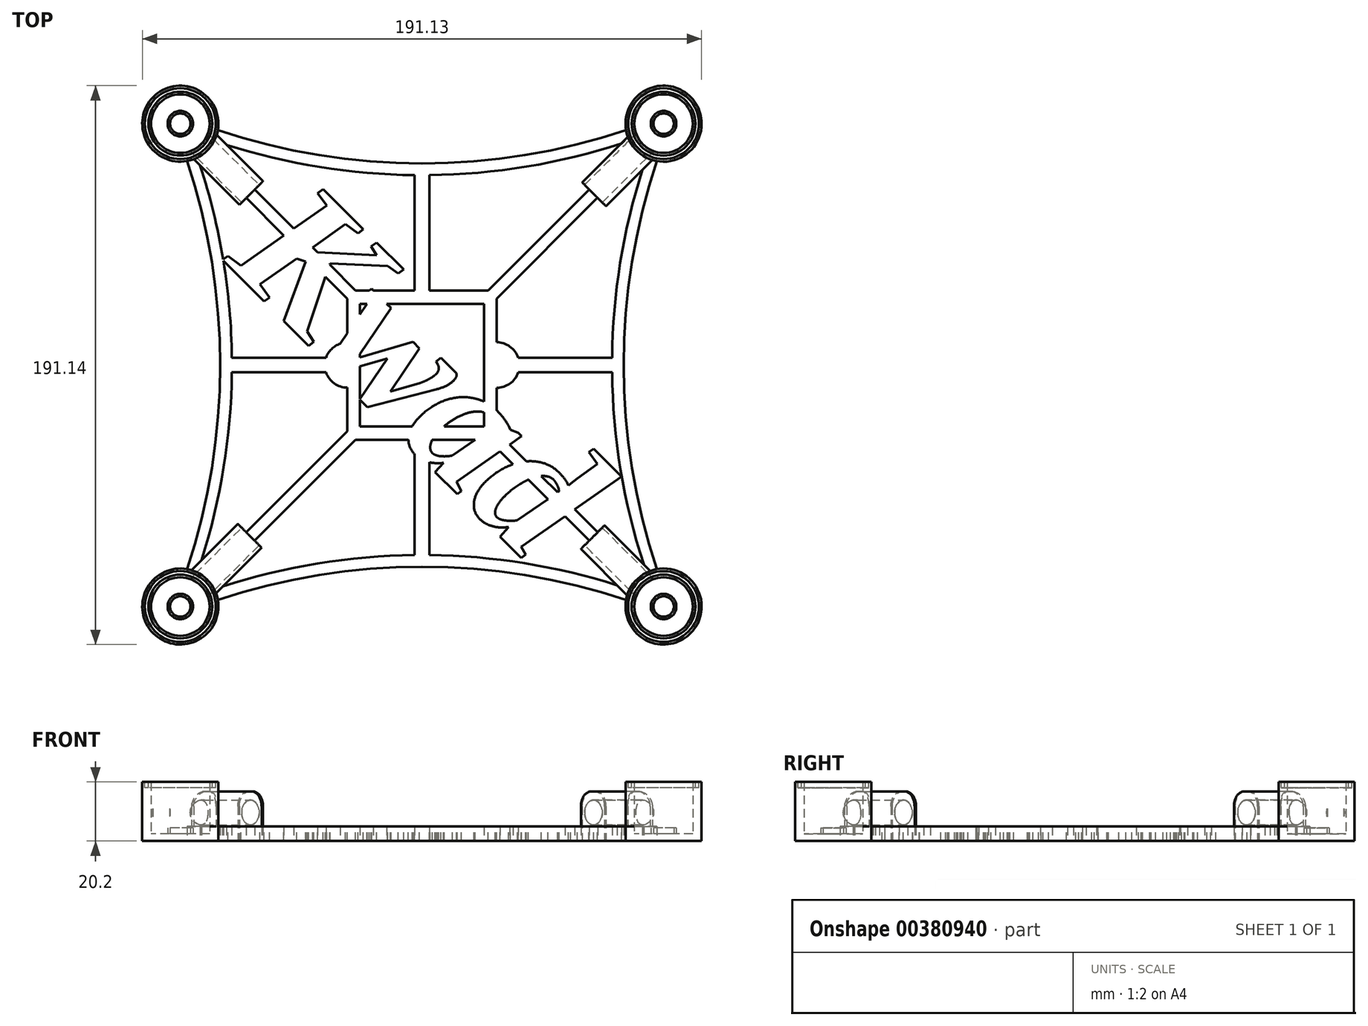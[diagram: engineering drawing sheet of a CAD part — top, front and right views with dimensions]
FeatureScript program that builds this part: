
annotation { "Feature Type Name" : "Feature", "Feature Type Description" : "" }
export const myFeature = defineFeature(function(context is Context, id is Id, definition is map)
    precondition{}
    {
        {
            var Q0;
            Q0=qCreatedBy(makeId("Top.planeOp"),FACE);
            var sketch = newSketch(context, id + "F0", { "sketchPlane" : qUnion([Q0])});
            skLineSegment(sketch, "E0.bottom", {"start": v(25.5, -25.5) * mm, "end": v(-25.5, -25.5) * mm});
            skLineSegment(sketch, "E0.top", {"start": v(25.5, 25.5) * mm, "end": v(-25.5, 25.5) * mm});
            skLineSegment(sketch, "E0.left", {"start": v(25.5, -25.5) * mm, "end": v(25.5, -7.8) * mm});
            skLineSegment(sketch, "E0.right", {"start": v(-25.5, -25.5) * mm, "end": v(-25.5, -7.7) * mm});
            skPoint(sketch, "E0.middle", {"position": v(0, 0) * mm});
            skCircle(sketch, "E1", {"center": v(-82.55, -82.57) * mm, "radius": 10 * mm});
            skArc(sketch, "E2", {"start": v(-70.95, -76.72) * mm, "mid": v(-73.36, -73.38) * mm, "end": v(-76.7, -70.96) * mm});
            skCircle(sketch, "E3", {"center": v(-82.55, -82.57) * mm, "radius": 3.5 * mm});
            skCircle(sketch, "E4", {"center": v(-82.55, -82.57) * mm, "radius": 4.36 * mm});
            skCircle(sketch, "E5.1.0", {"center": v(82.58, -82.57) * mm, "radius": 4.36 * mm});
            skArc(sketch, "E5.1.1", {"start": v(69.78, -80.31) * mm, "mid": v(91.78, -91.76) * mm, "end": v(80.33, -69.77) * mm});
            skCircle(sketch, "E5.1.2", {"center": v(82.58, -82.57) * mm, "radius": 3.5 * mm});
            skCircle(sketch, "E5.1.3", {"center": v(82.58, -82.57) * mm, "radius": 10 * mm});
            skCircle(sketch, "E5.2.0", {"center": v(82.58, 82.57) * mm, "radius": 4.36 * mm});
            skArc(sketch, "E5.2.1", {"start": v(80.33, 69.77) * mm, "mid": v(91.78, 91.76) * mm, "end": v(69.78, 80.31) * mm});
            skCircle(sketch, "E5.2.2", {"center": v(82.58, 82.57) * mm, "radius": 3.5 * mm});
            skCircle(sketch, "E5.2.3", {"center": v(82.58, 82.57) * mm, "radius": 10 * mm});
            skCircle(sketch, "E5.3.0", {"center": v(-82.55, 82.57) * mm, "radius": 4.36 * mm});
            skArc(sketch, "E5.3.1", {"start": v(-69.75, 80.31) * mm, "mid": v(-91.75, 91.76) * mm, "end": v(-80.3, 69.77) * mm});
            skCircle(sketch, "E5.3.2", {"center": v(-82.55, 82.57) * mm, "radius": 3.5 * mm});
            skCircle(sketch, "E5.3.3", {"center": v(-82.55, 82.57) * mm, "radius": 10 * mm});
            skPoint(sketch, "E5.center", {"position": v(0.01, 0) * mm});
            skPoint(sketch, "E6.endSnap0", {"position": v(-25.5, 0) * mm});
            skArc(sketch, "E7.trimOffspring", {"start": v(-70.95, 76.72) * mm, "mid": v(-37.18, 68.12) * mm, "end": v(-2.49, 64.97) * mm});
            skArc(sketch, "E8.trimOffspring", {"start": v(-69.75, 80.31) * mm, "mid": v(0.01, 68.95) * mm, "end": v(69.78, 80.31) * mm});
            skArc(sketch, "E9.trimOffspring", {"start": v(-80.3, -69.77) * mm, "mid": v(-68.94, 0) * mm, "end": v(-80.3, 69.77) * mm});
            skArc(sketch, "E10.trimOffspring", {"start": v(-76.7, -70.96) * mm, "mid": v(-68.1, -37.2) * mm, "end": v(-64.95, -2.5) * mm});
            skArc(sketch, "E11.trimOffspring", {"start": v(80.33, 69.77) * mm, "mid": v(68.96, 0) * mm, "end": v(80.33, -69.77) * mm});
            skArc(sketch, "E12.trimOffspring", {"start": v(76.73, 70.96) * mm, "mid": v(68.13, 37.2) * mm, "end": v(64.98, 2.5) * mm});
            skArc(sketch, "E13.trimOffspring", {"start": v(70.97, -76.72) * mm, "mid": v(37.21, -68.12) * mm, "end": v(2.51, -64.96) * mm});
            skArc(sketch, "E14.trimOffspring", {"start": v(69.78, -80.31) * mm, "mid": v(0.01, -68.95) * mm, "end": v(-69.75, -80.31) * mm});
            skArc(sketch, "E15.trimOffspring", {"start": v(76.73, -70.96) * mm, "mid": v(73.4, -73.38) * mm, "end": v(70.97, -76.72) * mm});
            skArc(sketch, "E16.trimOffspring", {"start": v(-80.3, -69.77) * mm, "mid": v(-91.75, -91.76) * mm, "end": v(-69.75, -80.31) * mm});
            skArc(sketch, "E17.trimOffspring", {"start": v(70.97, 76.72) * mm, "mid": v(73.4, 73.38) * mm, "end": v(76.73, 70.96) * mm});
            skArc(sketch, "E18.trimOffspring", {"start": v(-76.7, 70.96) * mm, "mid": v(-73.36, 73.38) * mm, "end": v(-70.95, 76.72) * mm});
            skLineSegment(sketch, "E19.0", {"start": v(-25.47, 2.5) * mm, "end": v(-25.5, 2.5) * mm});
            skLineSegment(sketch, "E20.0", {"start": v(-25.47, -2.5) * mm, "end": v(-25.5, -2.5) * mm});
            skLineSegment(sketch, "E21.1.0", {"start": v(-2.49, -25.49) * mm, "end": v(-2.49, -64.96) * mm});
            skLineSegment(sketch, "E21.1.1", {"start": v(2.51, -25.49) * mm, "end": v(2.51, -64.96) * mm});
            skLineSegment(sketch, "E21.2.0", {"start": v(32.9, -2.5) * mm, "end": v(64.98, -2.5) * mm});
            skLineSegment(sketch, "E21.2.1", {"start": v(32.9, 2.5) * mm, "end": v(64.98, 2.5) * mm});
            skLineSegment(sketch, "E21.3.0", {"start": v(2.51, 25.49) * mm, "end": v(2.51, 64.97) * mm});
            skLineSegment(sketch, "E21.3.1", {"start": v(-2.49, 25.49) * mm, "end": v(-2.49, 64.97) * mm});
            skArc(sketch, "E22.trimOffspring", {"start": v(-64.95, 2.5) * mm, "mid": v(-68.1, 37.2) * mm, "end": v(-76.7, 70.96) * mm});
            skArc(sketch, "E23.trimOffspring", {"start": v(64.98, -2.5) * mm, "mid": v(68.13, -37.2) * mm, "end": v(76.73, -70.96) * mm});
            skArc(sketch, "E24.trimOffspring", {"start": v(2.51, 64.97) * mm, "mid": v(37.21, 68.12) * mm, "end": v(70.97, 76.72) * mm});
            skArc(sketch, "E25.trimOffspring", {"start": v(-2.49, -64.96) * mm, "mid": v(-37.18, -68.12) * mm, "end": v(-70.95, -76.72) * mm});
            skLineSegment(sketch, "E26.bottom", {"start": v(21.19, -20.94) * mm, "end": v(-21.16, -20.94) * mm});
            skLineSegment(sketch, "E26.top", {"start": v(21.19, 20.94) * mm, "end": v(-21.16, 20.94) * mm});
            skLineSegment(sketch, "E26.left", {"start": v(21.19, -20.94) * mm, "end": v(21.19, 20.94) * mm});
            skLineSegment(sketch, "E26.right", {"start": v(-21.16, -20.94) * mm, "end": v(-21.16, 20.94) * mm});
            skArc(sketch, "E27", {"start": v(-25.5, 7.7) * mm, "mid": v(-29.97, 6.27) * mm, "end": v(-32.78, 2.5) * mm});
            skArc(sketch, "E28", {"start": v(25.5, 7.8) * mm, "mid": v(30.05, 6.34) * mm, "end": v(32.9, 2.5) * mm});
            skLineSegment(sketch, "E29.trimOffspring", {"start": v(-32.78, 2.5) * mm, "end": v(-64.95, 2.5) * mm});
            skLineSegment(sketch, "E30.trimOffspring", {"start": v(-32.78, -2.5) * mm, "end": v(-64.95, -2.5) * mm});
            skLineSegment(sketch, "E31.trimOffspring", {"start": v(-25.5, 7.7) * mm, "end": v(-25.5, 25.5) * mm});
            skArc(sketch, "E32.trimOffspring", {"start": v(-32.78, -2.5) * mm, "mid": v(-29.97, -6.27) * mm, "end": v(-25.5, -7.7) * mm});
            skLineSegment(sketch, "E33.trimOffspring", {"start": v(25.5, 7.8) * mm, "end": v(25.5, 25.5) * mm});
            skPoint(sketch, "E34.orphan", {"position": v(25.5, -2.5) * mm});
            skPoint(sketch, "E35.orphan", {"position": v(25.5, 2.5) * mm});
            skArc(sketch, "E36.trimOffspring", {"start": v(32.9, -2.5) * mm, "mid": v(30.05, -6.34) * mm, "end": v(25.5, -7.8) * mm});
            skSolve(sketch);
        }
        {
            var Q0;
            Q0=makeQuery(id+"F0.imprint","IMPRINT",FACE,{"disambiguationData":[TD([[makeQuery(id+"F0.imprint","IMPRINT",EDGE,{"derivedFrom":sQuery(id+"F0.wireOp",EDGE,"E1")}),-1.0]])]});
            var Q1;
            Q1=makeQuery(id+"F0.imprint","IMPRINT",FACE,{"disambiguationData":[TD([[makeQuery(id+"F0.imprint","IMPRINT",EDGE,{"derivedFrom":sQuery(id+"F0.wireOp",EDGE,"E26.bottom")}),1.0]])]});
            extrude(context, id + "F1", {"entities" : qUnion([Q0, Q1]), "depth" : 5 * mm});
        }
        {
            var Q0;
            Q0=makeQuery(id+"F0.imprint","IMPRINT",FACE,{"disambiguationData":[TD([[makeQuery(id+"F0.imprint","IMPRINT",EDGE,{"derivedFrom":sQuery(id+"F0.wireOp",EDGE,"E1")}),1.0]])]});
            var Q1;
            Q1=makeQuery(id+"F0.imprint","IMPRINT",FACE,{"disambiguationData":[TD([[makeQuery(id+"F0.imprint","IMPRINT",EDGE,{"derivedFrom":sQuery(id+"F0.wireOp",EDGE,"E3")}),1.0]])]});
            var Q2;
            Q2=makeQuery(id+"F0.imprint","IMPRINT",FACE,{"disambiguationData":[TD([[makeQuery(id+"F0.imprint","IMPRINT",EDGE,{"derivedFrom":sQuery(id+"F0.wireOp",EDGE,"E3")}),-1.0]])]});
            var Q3;
            Q3=makeQuery(id+"F0.imprint","IMPRINT",FACE,{"disambiguationData":[TD([[makeQuery(id+"F0.imprint","IMPRINT",EDGE,{"derivedFrom":sQuery(id+"F0.wireOp",EDGE,"E5.1.0")}),-1.0]])]});
            var Q4;
            Q4=makeQuery(id+"F0.imprint","IMPRINT",FACE,{"disambiguationData":[TD([[makeQuery(id+"F0.imprint","IMPRINT",EDGE,{"derivedFrom":sQuery(id+"F0.wireOp",EDGE,"E5.1.2")}),1.0]])]});
            var Q5;
            Q5=makeQuery(id+"F0.imprint","IMPRINT",FACE,{"disambiguationData":[TD([[makeQuery(id+"F0.imprint","IMPRINT",EDGE,{"derivedFrom":sQuery(id+"F0.wireOp",EDGE,"E5.1.0")}),1.0]])]});
            var Q6;
            Q6=makeQuery(id+"F0.imprint","IMPRINT",FACE,{"disambiguationData":[TD([[makeQuery(id+"F0.imprint","IMPRINT",EDGE,{"derivedFrom":sQuery(id+"F0.wireOp",EDGE,"E5.2.0")}),-1.0]])]});
            var Q7;
            Q7=makeQuery(id+"F0.imprint","IMPRINT",FACE,{"disambiguationData":[TD([[makeQuery(id+"F0.imprint","IMPRINT",EDGE,{"derivedFrom":sQuery(id+"F0.wireOp",EDGE,"E5.2.2")}),1.0]])]});
            var Q8;
            Q8=makeQuery(id+"F0.imprint","IMPRINT",FACE,{"disambiguationData":[TD([[makeQuery(id+"F0.imprint","IMPRINT",EDGE,{"derivedFrom":sQuery(id+"F0.wireOp",EDGE,"E5.2.0")}),1.0]])]});
            var Q9;
            Q9=makeQuery(id+"F0.imprint","IMPRINT",FACE,{"disambiguationData":[TD([[makeQuery(id+"F0.imprint","IMPRINT",EDGE,{"derivedFrom":sQuery(id+"F0.wireOp",EDGE,"E5.3.0")}),-1.0]])]});
            var Q10;
            Q10=makeQuery(id+"F0.imprint","IMPRINT",FACE,{"disambiguationData":[TD([[makeQuery(id+"F0.imprint","IMPRINT",EDGE,{"derivedFrom":sQuery(id+"F0.wireOp",EDGE,"E5.3.2")}),1.0]])]});
            var Q11;
            Q11=makeQuery(id+"F0.imprint","IMPRINT",FACE,{"disambiguationData":[TD([[makeQuery(id+"F0.imprint","IMPRINT",EDGE,{"derivedFrom":sQuery(id+"F0.wireOp",EDGE,"E5.3.0")}),1.0]])]});
            extrude(context, id + "F2", {"entities" : qUnion([Q0, Q1, Q2, Q3, Q4, Q5, Q6, Q7, Q8, Q9, Q10, Q11]), "operationType" : NewBodyOperationType.ADD, "depth" : 2.5 * mm});
        }
        {
            var Q0;
            Q0=makeQuery(id+"F0.imprint","IMPRINT",FACE,{"disambiguationData":[TD([[makeQuery(id+"F0.imprint","IMPRINT",EDGE,{"derivedFrom":sQuery(id+"F0.wireOp",EDGE,"E5.1.0")}),1.0]])]});
            var Q1;
            Q1=makeQuery(id+"F0.imprint","IMPRINT",FACE,{"disambiguationData":[TD([[makeQuery(id+"F0.imprint","IMPRINT",EDGE,{"derivedFrom":sQuery(id+"F0.wireOp",EDGE,"E3")}),-1.0]])]});
            var Q2;
            Q2=makeQuery(id+"F0.imprint","IMPRINT",FACE,{"disambiguationData":[TD([[makeQuery(id+"F0.imprint","IMPRINT",EDGE,{"derivedFrom":sQuery(id+"F0.wireOp",EDGE,"E5.3.0")}),1.0]])]});
            var Q3;
            Q3=makeQuery(id+"F0.imprint","IMPRINT",FACE,{"disambiguationData":[TD([[makeQuery(id+"F0.imprint","IMPRINT",EDGE,{"derivedFrom":sQuery(id+"F0.wireOp",EDGE,"E5.2.0")}),1.0]])]});
            extrude(context, id + "F3", {"entities" : qUnion([Q0, Q1, Q2, Q3]), "operationType" : NewBodyOperationType.ADD, "depth" : 4.5 * mm});
        }
        {
            var Q0;
            Q0=makeQuery(id+"F1.opExtrude","CAP_FACE",FACE,{"disambiguationData":[OSD([sQuery(id+"F0.wireOp",EDGE,"E0.bottom"),sQuery(id+"F0.wireOp",EDGE,"E0.top"),sQuery(id+"F0.wireOp",EDGE,"E0.left"),sQuery(id+"F0.wireOp",EDGE,"E0.right"),sQuery(id+"F0.wireOp",EDGE,"E1"),sQuery(id+"F0.wireOp",EDGE,"E2"),sQuery(id+"F0.wireOp",EDGE,"E5.1.1"),sQuery(id+"F0.wireOp",EDGE,"E5.1.3"),sQuery(id+"F0.wireOp",EDGE,"E5.2.1"),sQuery(id+"F0.wireOp",EDGE,"E5.2.3"),sQuery(id+"F0.wireOp",EDGE,"E5.3.1"),sQuery(id+"F0.wireOp",EDGE,"E5.3.3"),sQuery(id+"F0.wireOp",EDGE,"E7.trimOffspring"),sQuery(id+"F0.wireOp",EDGE,"E8.trimOffspring"),sQuery(id+"F0.wireOp",EDGE,"E9.trimOffspring"),sQuery(id+"F0.wireOp",EDGE,"E10.trimOffspring"),sQuery(id+"F0.wireOp",EDGE,"E11.trimOffspring"),sQuery(id+"F0.wireOp",EDGE,"E12.trimOffspring"),sQuery(id+"F0.wireOp",EDGE,"E13.trimOffspring"),sQuery(id+"F0.wireOp",EDGE,"E14.trimOffspring"),sQuery(id+"F0.wireOp",EDGE,"E15.trimOffspring"),sQuery(id+"F0.wireOp",EDGE,"E16.trimOffspring"),sQuery(id+"F0.wireOp",EDGE,"E17.trimOffspring"),sQuery(id+"F0.wireOp",EDGE,"E18.trimOffspring"),sQuery(id+"F0.wireOp",EDGE,"E19.0"),sQuery(id+"F0.wireOp",EDGE,"E20.0"),sQuery(id+"F0.wireOp",EDGE,"E21.1.0"),sQuery(id+"F0.wireOp",EDGE,"E21.1.1"),sQuery(id+"F0.wireOp",EDGE,"E21.2.0"),sQuery(id+"F0.wireOp",EDGE,"E21.2.1"),sQuery(id+"F0.wireOp",EDGE,"E21.3.0"),sQuery(id+"F0.wireOp",EDGE,"E21.3.1"),sQuery(id+"F0.wireOp",EDGE,"E22.trimOffspring"),sQuery(id+"F0.wireOp",EDGE,"E23.trimOffspring"),sQuery(id+"F0.wireOp",EDGE,"E24.trimOffspring"),sQuery(id+"F0.wireOp",EDGE,"E25.trimOffspring"),sQuery(id+"F0.wireOp",EDGE,"E26.bottom"),sQuery(id+"F0.wireOp",EDGE,"E26.top"),sQuery(id+"F0.wireOp",EDGE,"E26.left"),sQuery(id+"F0.wireOp",EDGE,"E26.right")])],"isStart":false});
            var sketch = newSketch(context, id + "F4", { "sketchPlane" : qUnion([Q0])});
            skCircle(sketch, "E37", {"center": v(-82.55, 82.57) * mm, "radius": 10 * mm});
            skCircle(sketch, "E38", {"center": v(-82.55, 82.57) * mm, "radius": 13 * mm});
            skPoint(sketch, "E39.center", {"position": v(0, 0) * mm});
            skCircle(sketch, "E40", {"center": v(82.58, 82.57) * mm, "radius": 10 * mm});
            skCircle(sketch, "E41", {"center": v(82.58, 82.57) * mm, "radius": 13 * mm});
            skCircle(sketch, "E42", {"center": v(82.58, -82.57) * mm, "radius": 10 * mm});
            skCircle(sketch, "E43", {"center": v(82.58, -82.57) * mm, "radius": 13 * mm});
            skCircle(sketch, "E44", {"center": v(-82.55, -82.57) * mm, "radius": 10 * mm});
            skCircle(sketch, "E45", {"center": v(-82.55, -82.57) * mm, "radius": 13 * mm});
            skSolve(sketch);
        }
        {
            var Q0;
            Q0 = qSketchRegion(id + "F4", true);
            extrude(context, id + "F5", {"entities" : qUnion([Q0]), "operationType" : NewBodyOperationType.ADD, "depth" : 15.2 * mm});
        }
        {
            var Q0;
            Q0=makeQuery(id+"F5.opExtrude","CAP_FACE",FACE,{"disambiguationData":[OSD([sQuery(id+"F4.wireOp",EDGE,"E37"),sQuery(id+"F4.wireOp",EDGE,"E38")])],"isStart":false});
            var sketch = newSketch(context, id + "F6", { "sketchPlane" : qUnion([Q0])});
            skCircle(sketch, "E46", {"center": v(-82.55, 82.57) * mm, "radius": 12.1 * mm});
            skCircle(sketch, "E47", {"center": v(-82.55, 82.57) * mm, "radius": 10.9 * mm});
            skCircle(sketch, "E48.1.0", {"center": v(-82.57, -82.55) * mm, "radius": 10.9 * mm});
            skCircle(sketch, "E48.1.1", {"center": v(-82.57, -82.55) * mm, "radius": 12.1 * mm});
            skCircle(sketch, "E48.2.0", {"center": v(82.55, -82.57) * mm, "radius": 10.9 * mm});
            skCircle(sketch, "E48.2.1", {"center": v(82.55, -82.57) * mm, "radius": 12.1 * mm});
            skCircle(sketch, "E48.3.0", {"center": v(82.57, 82.55) * mm, "radius": 10.9 * mm});
            skCircle(sketch, "E48.3.1", {"center": v(82.57, 82.55) * mm, "radius": 12.1 * mm});
            skPoint(sketch, "E48.center", {"position": v(0, 0) * mm});
            skSolve(sketch);
        }
        {
            var Q0;
            Q0 = qSketchRegion(id + "F6", true);
            extrude(context, id + "F7", {"entities" : qUnion([Q0]), "operationType" : NewBodyOperationType.REMOVE, "oppositeDirection" : true, "depth" : 2 * mm});
        }
        {
            var Q0;
            Q0=makeQuery(id+"F1.opExtrude","SWEPT_EDGE",EDGE,{"disambiguationData":[OSD([sQuery(id+"F0.wireOp",EDGE,"E12.trimOffspring"),sQuery(id+"F0.wireOp",EDGE,"E17.trimOffspring")])]});
            var Q1;
            Q1=makeQuery(id+"F1.opExtrude","SWEPT_EDGE",EDGE,{"disambiguationData":[OSD([sQuery(id+"F0.wireOp",EDGE,"E17.trimOffspring"),sQuery(id+"F0.wireOp",EDGE,"E24.trimOffspring")])]});
            cPlane(context, id + "F8", {"entities" : qUnion([Q0, Q1]), "cplaneType" : CPlaneType.LINE_ANGLE, "offset" : 25.4 * mm, "angle" : 0 * degree, "width" : 152.4 * mm, "height" : 152.4 * mm});
        }
        {
            var Q0;
            Q0=qCreatedBy(id+"F8.planeOp",FACE);
            var sketch = newSketch(context, id + "F9", { "sketchPlane" : qUnion([Q0])});
            skLineSegment(sketch, "E49", {"start": v(0, 0) * mm, "end": v(0, 5.5) * mm});
            skLineSegment(sketch, "E50", {"start": v(0, 5.5) * mm, "end": v(0, 9.75) * mm});
            skCircle(sketch, "E51", {"center": v(0, 9.75) * mm, "radius": 4.25 * mm});
            skSolve(sketch);
        }
        {
            var Q0;
            Q0=makeQuery(id+"F1.opExtrude","SWEPT_EDGE",EDGE,{"disambiguationData":[OSD([sQuery(id+"F0.wireOp",EDGE,"E15.trimOffspring"),sQuery(id+"F0.wireOp",EDGE,"E23.trimOffspring")])]});
            var Q1;
            Q1=makeQuery(id+"F1.opExtrude","SWEPT_EDGE",EDGE,{"disambiguationData":[OSD([sQuery(id+"F0.wireOp",EDGE,"E13.trimOffspring"),sQuery(id+"F0.wireOp",EDGE,"E15.trimOffspring")])]});
            cPlane(context, id + "F10", {"entities" : qUnion([Q0, Q1]), "cplaneType" : CPlaneType.LINE_ANGLE, "offset" : 25.4 * mm, "angle" : 0 * degree, "width" : 152.4 * mm, "height" : 152.4 * mm});
        }
        {
            var Q0;
            Q0=qCreatedBy(id+"F10.planeOp",FACE);
            var sketch = newSketch(context, id + "F11", { "sketchPlane" : qUnion([Q0])});
            skCircle(sketch, "E52", {"center": v(0, 9.75) * mm, "radius": 4.25 * mm});
            skLineSegment(sketch, "E53", {"start": v(0, 0) * mm, "end": v(0, 5.5) * mm});
            skLineSegment(sketch, "E54", {"start": v(0, 5.5) * mm, "end": v(0, 9.75) * mm});
            skSolve(sketch);
        }
        {
            var Q0;
            Q0=makeQuery(id+"F1.opExtrude","SWEPT_EDGE",EDGE,{"disambiguationData":[OSD([sQuery(id+"F0.wireOp",EDGE,"E7.trimOffspring"),sQuery(id+"F0.wireOp",EDGE,"E18.trimOffspring")])]});
            var Q1;
            Q1=makeQuery(id+"F1.opExtrude","SWEPT_EDGE",EDGE,{"disambiguationData":[OSD([sQuery(id+"F0.wireOp",EDGE,"E18.trimOffspring"),sQuery(id+"F0.wireOp",EDGE,"E22.trimOffspring")])]});
            cPlane(context, id + "F12", {"entities" : qUnion([Q0, Q1]), "cplaneType" : CPlaneType.LINE_ANGLE, "offset" : 25.4 * mm, "angle" : 0 * degree, "width" : 152.4 * mm, "height" : 152.4 * mm});
        }
        {
            var Q0;
            Q0=qCreatedBy(id+"F12.planeOp",FACE);
            var sketch = newSketch(context, id + "F13", { "sketchPlane" : qUnion([Q0])});
            skLineSegment(sketch, "E55", {"start": v(0, 0) * mm, "end": v(0, 5.5) * mm});
            skLineSegment(sketch, "E56", {"start": v(0, 5.5) * mm, "end": v(0, 9.75) * mm});
            skCircle(sketch, "E57", {"center": v(0, 9.75) * mm, "radius": 4.25 * mm});
            skSolve(sketch);
        }
        {
            var Q0;
            Q0=makeQuery(id+"F1.opExtrude","SWEPT_EDGE",EDGE,{"disambiguationData":[OSD([sQuery(id+"F0.wireOp",EDGE,"E2"),sQuery(id+"F0.wireOp",EDGE,"E10.trimOffspring")])]});
            var Q1;
            Q1=makeQuery(id+"F1.opExtrude","SWEPT_EDGE",EDGE,{"disambiguationData":[OSD([sQuery(id+"F0.wireOp",EDGE,"E2"),sQuery(id+"F0.wireOp",EDGE,"E25.trimOffspring")])]});
            cPlane(context, id + "F14", {"entities" : qUnion([Q0, Q1]), "cplaneType" : CPlaneType.LINE_ANGLE, "offset" : 25.4 * mm, "angle" : 0 * degree, "width" : 152.4 * mm, "height" : 152.4 * mm});
        }
        {
            var Q0;
            Q0=qCreatedBy(id+"F14.planeOp",FACE);
            var sketch = newSketch(context, id + "F15", { "sketchPlane" : qUnion([Q0])});
            skLineSegment(sketch, "E58", {"start": v(0, 0) * mm, "end": v(0, 5.5) * mm});
            skLineSegment(sketch, "E59", {"start": v(0, 5.5) * mm, "end": v(0, 9.75) * mm});
            skCircle(sketch, "E60", {"center": v(0, 9.75) * mm, "radius": 4.25 * mm});
            skSolve(sketch);
        }
        {
            var Q0;
            Q0 = qSketchRegion(id + "F13", true);
            extrude(context, id + "F16", {"entities" : qUnion([Q0]), "operationType" : NewBodyOperationType.REMOVE, "endBound" : BoundingType.SYMMETRIC, "oppositeDirection" : true, "depth" : 43 * mm});
        }
        {
            var Q0;
            Q0 = qSketchRegion(id + "F15", true);
            extrude(context, id + "F17", {"entities" : qUnion([Q0]), "operationType" : NewBodyOperationType.REMOVE, "endBound" : BoundingType.SYMMETRIC, "oppositeDirection" : true, "depth" : 7 * mm});
        }
        {
            var Q0;
            Q0 = qSketchRegion(id + "F11", true);
            extrude(context, id + "F18", {"entities" : qUnion([Q0]), "operationType" : NewBodyOperationType.REMOVE, "endBound" : BoundingType.SYMMETRIC, "oppositeDirection" : true, "depth" : 7 * mm});
        }
        {
            var Q0;
            Q0 = qSketchRegion(id + "F9", true);
            extrude(context, id + "F19", {"entities" : qUnion([Q0]), "operationType" : NewBodyOperationType.REMOVE, "endBound" : BoundingType.SYMMETRIC, "oppositeDirection" : true, "depth" : 7 * mm});
        }
        {
            var Q0;
            {var subQ16=sQuery(id+"F0.wireOp",EDGE,"E0.left");Q0=makeQuery(id+"F0.imprint","IMPRINT",FACE,{"disambiguationData":[TD([[makeQuery(id+"F0.imprint","IMPRINT",EDGE,{"derivedFrom":subQ16}),1.0]])]});}
            var sketch = newSketch(context, id + "F20", { "sketchPlane" : qUnion([Q0])});
            skLineSegment(sketch, "E61", {"start": v(-70.95, -76.72) * mm, "end": v(-76.7, -70.96) * mm});
            skLineSegment(sketch, "E62", {"start": v(70.97, -76.72) * mm, "end": v(76.73, -70.96) * mm});
            skLineSegment(sketch, "E63.0", {"start": v(55.42, -61.16) * mm, "end": v(61.18, -55.4) * mm});
            skLineSegment(sketch, "E64.0", {"start": v(54.8, 62.42) * mm, "end": v(60.55, 56.68) * mm});
            skLineSegment(sketch, "E65", {"start": v(78.75, 70.15) * mm, "end": v(62.91, 54.32) * mm});
            skLineSegment(sketch, "E66", {"start": v(62.91, 54.32) * mm, "end": v(60.55, 56.68) * mm});
            skLineSegment(sketch, "E67", {"start": v(70.4, 78.02) * mm, "end": v(54.8, 62.42) * mm});
            skLineSegment(sketch, "E68.1.0", {"start": v(-78, 70.4) * mm, "end": v(-62.4, 54.8) * mm});
            skLineSegment(sketch, "E68.1.1", {"start": v(-70.13, 78.73) * mm, "end": v(-54.3, 62.9) * mm});
            skLineSegment(sketch, "E68.1.2", {"start": v(-62.4, 54.8) * mm, "end": v(-62.52, 54.67) * mm});
            skLineSegment(sketch, "E68.1.3", {"start": v(-62.52, 54.67) * mm, "end": v(-56.66, 60.53) * mm});
            skLineSegment(sketch, "E68.1.4", {"start": v(-54.3, 62.9) * mm, "end": v(-56.66, 60.53) * mm});
            skLineSegment(sketch, "E68.1.5", {"start": v(-76.59, 71.8) * mm, "end": v(-70.13, 78.73) * mm});
            skLineSegment(sketch, "E68.1.6", {"start": v(-76.59, 71.8) * mm, "end": v(-78, 70.4) * mm});
            skLineSegment(sketch, "E68.1.7", {"start": v(-70.13, 78.73) * mm, "end": v(-70.13, 78.73) * mm});
            skLineSegment(sketch, "E68.2.0", {"start": v(-70.38, -78.02) * mm, "end": v(-54.78, -62.42) * mm});
            skLineSegment(sketch, "E68.2.1", {"start": v(-78.72, -70.15) * mm, "end": v(-62.89, -54.32) * mm});
            skLineSegment(sketch, "E68.2.2", {"start": v(-54.78, -62.42) * mm, "end": v(-54.66, -62.54) * mm});
            skLineSegment(sketch, "E68.2.3", {"start": v(-54.66, -62.54) * mm, "end": v(-60.52, -56.68) * mm});
            skLineSegment(sketch, "E68.2.4", {"start": v(-62.89, -54.32) * mm, "end": v(-60.52, -56.68) * mm});
            skLineSegment(sketch, "E68.2.5", {"start": v(-71.8, -76.6) * mm, "end": v(-78.72, -70.15) * mm});
            skLineSegment(sketch, "E68.2.6", {"start": v(-71.8, -76.6) * mm, "end": v(-70.38, -78.02) * mm});
            skLineSegment(sketch, "E68.2.7", {"start": v(-78.72, -70.15) * mm, "end": v(-78.72, -70.15) * mm});
            skLineSegment(sketch, "E68.3.0", {"start": v(78.03, -70.4) * mm, "end": v(62.43, -54.8) * mm});
            skLineSegment(sketch, "E68.3.1", {"start": v(70.16, -78.73) * mm, "end": v(54.33, -62.9) * mm});
            skLineSegment(sketch, "E68.3.2", {"start": v(62.43, -54.8) * mm, "end": v(62.55, -54.67) * mm});
            skLineSegment(sketch, "E68.3.3", {"start": v(62.55, -54.67) * mm, "end": v(56.7, -60.53) * mm});
            skLineSegment(sketch, "E68.3.4", {"start": v(54.33, -62.9) * mm, "end": v(56.7, -60.53) * mm});
            skLineSegment(sketch, "E68.3.5", {"start": v(76.62, -71.8) * mm, "end": v(70.16, -78.73) * mm});
            skLineSegment(sketch, "E68.3.6", {"start": v(76.62, -71.8) * mm, "end": v(78.03, -70.4) * mm});
            skLineSegment(sketch, "E68.3.7", {"start": v(70.16, -78.73) * mm, "end": v(70.16, -78.73) * mm});
            skPoint(sketch, "E68.center", {"position": v(0.01, 0) * mm});
            skPoint(sketch, "E69.orphan", {"position": v(54.69, 62.54) * mm});
            skLineSegment(sketch, "E70", {"start": v(70.4, 78.02) * mm, "end": v(78.75, 70.15) * mm});
            skSolve(sketch);
        }
        {
            var Q0;
            Q0 = qSketchRegion(id + "F20", true);
            extrude(context, id + "F21", {"entities" : qUnion([Q0]), "operationType" : NewBodyOperationType.ADD, "depth" : 17 * mm});
        }
        {
            var Q0;
            Q0=makeQuery(id+"F21.opExtrude","SWEPT_FACE",FACE,{"disambiguationData":[OSD([sQuery(id+"F20.wireOp",EDGE,"E68.1.3")])]});
            var sketch = newSketch(context, id + "F22", { "sketchPlane" : qUnion([Q0])});
            skCircle(sketch, "E71", {"center": v(0, 9.75) * mm, "radius": 4.25 * mm});
            skSolve(sketch);
        }
        {
            var Q0;
            Q0=makeQuery(id+"F21.opExtrude","SWEPT_FACE",FACE,{"disambiguationData":[OSD([sQuery(id+"F20.wireOp",EDGE,"E68.2.3")])]});
            var sketch = newSketch(context, id + "F23", { "sketchPlane" : qUnion([Q0])});
            skCircle(sketch, "E72", {"center": v(0, 9.75) * mm, "radius": 4.25 * mm});
            skSolve(sketch);
        }
        {
            var Q0;
            Q0=makeQuery(id+"F21.opExtrude","SWEPT_FACE",FACE,{"disambiguationData":[OSD([sQuery(id+"F20.wireOp",EDGE,"E68.3.3")])]});
            var sketch = newSketch(context, id + "F24", { "sketchPlane" : qUnion([Q0])});
            skCircle(sketch, "E73", {"center": v(0, 9.75) * mm, "radius": 4.25 * mm});
            skSolve(sketch);
        }
        {
            var Q0;
            Q0=makeQuery(id+"F21.opExtrude","SWEPT_FACE",FACE,{"disambiguationData":[OSD([sQuery(id+"F20.wireOp",EDGE,"E64.0")])]});
            var sketch = newSketch(context, id + "F25", { "sketchPlane" : qUnion([Q0])});
            skCircle(sketch, "E74", {"center": v(0, 9.75) * mm, "radius": 4.25 * mm});
            skSolve(sketch);
        }
        {
            var Q0;
            Q0 = qSketchRegion(id + "F22", true);
            extrude(context, id + "F26", {"entities" : qUnion([Q0]), "operationType" : NewBodyOperationType.REMOVE, "oppositeDirection" : true, "depth" : 25.4 * mm});
        }
        {
            var Q0;
            Q0 = qSketchRegion(id + "F23", true);
            extrude(context, id + "F27", {"entities" : qUnion([Q0]), "operationType" : NewBodyOperationType.REMOVE, "oppositeDirection" : true, "depth" : 25.4 * mm});
        }
        {
            var Q0;
            Q0 = qSketchRegion(id + "F24", true);
            extrude(context, id + "F28", {"entities" : qUnion([Q0]), "operationType" : NewBodyOperationType.REMOVE, "oppositeDirection" : true, "depth" : 25.4 * mm});
        }
        {
            var Q0;
            Q0 = qSketchRegion(id + "F25", true);
            extrude(context, id + "F29", {"entities" : qUnion([Q0]), "operationType" : NewBodyOperationType.REMOVE, "oppositeDirection" : true, "depth" : 25.4 * mm});
        }
        {
            var Q0;
            Q0=makeQuery(id+"F21.opExtrude","CAP_EDGE",EDGE,{"disambiguationData":[OSD([sQuery(id+"F20.wireOp",EDGE,"E68.2.1")])],"isStart":false});
            var Q1;
            Q1=makeQuery(id+"F21.opExtrude","CAP_EDGE",EDGE,{"disambiguationData":[OSD([sQuery(id+"F20.wireOp",EDGE,"E68.2.0")])],"isStart":false});
            fillet(context, id + "F30", {"entities" : qUnion([Q0, Q1]), "radius" : 5.08 * mm, "tangentPropagation" : true, "allowEdgeOverflow" : false});
        }
        {
            var Q0;
            Q0=makeQuery(id+"F21.opExtrude","CAP_EDGE",EDGE,{"disambiguationData":[OSD([sQuery(id+"F20.wireOp",EDGE,"E68.1.1")])],"isStart":false});
            var Q1;
            Q1=makeQuery(id+"F21.opExtrude","CAP_EDGE",EDGE,{"disambiguationData":[OSD([sQuery(id+"F20.wireOp",EDGE,"E68.1.0")])],"isStart":false});
            fillet(context, id + "F31", {"entities" : qUnion([Q0, Q1]), "radius" : 5.08 * mm, "tangentPropagation" : true, "allowEdgeOverflow" : false});
        }
        {
            var Q0;
            Q0=makeQuery(id+"F21.opExtrude","CAP_EDGE",EDGE,{"disambiguationData":[OSD([sQuery(id+"F20.wireOp",EDGE,"E68.3.1")])],"isStart":false});
            var Q1;
            Q1=makeQuery(id+"F21.opExtrude","CAP_EDGE",EDGE,{"disambiguationData":[OSD([sQuery(id+"F20.wireOp",EDGE,"E68.3.0")])],"isStart":false});
            var Q2;
            Q2=makeQuery(id+"F21.opExtrude","CAP_EDGE",EDGE,{"disambiguationData":[OSD([sQuery(id+"F20.wireOp",EDGE,"E67")])],"isStart":false});
            var Q3;
            Q3=makeQuery(id+"F21.opExtrude","CAP_EDGE",EDGE,{"disambiguationData":[OSD([sQuery(id+"F20.wireOp",EDGE,"E65")])],"isStart":false});
            fillet(context, id + "F32", {"entities" : qUnion([Q0, Q1, Q2, Q3]), "radius" : 5.08 * mm, "tangentPropagation" : true, "allowEdgeOverflow" : false});
        }
        {
            var Q0;
            Q0=makeQuery(id+"F1.opExtrude","CAP_FACE",FACE,{"disambiguationData":[OSD([sQuery(id+"F0.wireOp",EDGE,"E0.bottom"),sQuery(id+"F0.wireOp",EDGE,"E0.top"),sQuery(id+"F0.wireOp",EDGE,"E0.left"),sQuery(id+"F0.wireOp",EDGE,"E0.right"),sQuery(id+"F0.wireOp",EDGE,"E1"),sQuery(id+"F0.wireOp",EDGE,"E2"),sQuery(id+"F0.wireOp",EDGE,"E5.1.1"),sQuery(id+"F0.wireOp",EDGE,"E5.1.3"),sQuery(id+"F0.wireOp",EDGE,"E5.2.1"),sQuery(id+"F0.wireOp",EDGE,"E5.2.3"),sQuery(id+"F0.wireOp",EDGE,"E5.3.1"),sQuery(id+"F0.wireOp",EDGE,"E5.3.3"),sQuery(id+"F0.wireOp",EDGE,"E7.trimOffspring"),sQuery(id+"F0.wireOp",EDGE,"E8.trimOffspring"),sQuery(id+"F0.wireOp",EDGE,"E9.trimOffspring"),sQuery(id+"F0.wireOp",EDGE,"E10.trimOffspring"),sQuery(id+"F0.wireOp",EDGE,"E11.trimOffspring"),sQuery(id+"F0.wireOp",EDGE,"E12.trimOffspring"),sQuery(id+"F0.wireOp",EDGE,"E13.trimOffspring"),sQuery(id+"F0.wireOp",EDGE,"E14.trimOffspring"),sQuery(id+"F0.wireOp",EDGE,"E15.trimOffspring"),sQuery(id+"F0.wireOp",EDGE,"E16.trimOffspring"),sQuery(id+"F0.wireOp",EDGE,"E17.trimOffspring"),sQuery(id+"F0.wireOp",EDGE,"E18.trimOffspring"),sQuery(id+"F0.wireOp",EDGE,"E21.1.0"),sQuery(id+"F0.wireOp",EDGE,"E21.1.1"),sQuery(id+"F0.wireOp",EDGE,"E21.2.0"),sQuery(id+"F0.wireOp",EDGE,"E21.2.1"),sQuery(id+"F0.wireOp",EDGE,"E21.3.0"),sQuery(id+"F0.wireOp",EDGE,"E21.3.1"),sQuery(id+"F0.wireOp",EDGE,"E22.trimOffspring"),sQuery(id+"F0.wireOp",EDGE,"E23.trimOffspring"),sQuery(id+"F0.wireOp",EDGE,"E24.trimOffspring"),sQuery(id+"F0.wireOp",EDGE,"E25.trimOffspring"),sQuery(id+"F0.wireOp",EDGE,"E26.bottom"),sQuery(id+"F0.wireOp",EDGE,"E26.top"),sQuery(id+"F0.wireOp",EDGE,"E26.left"),sQuery(id+"F0.wireOp",EDGE,"E26.right"),sQuery(id+"F0.wireOp",EDGE,"E27"),sQuery(id+"F0.wireOp",EDGE,"E28"),sQuery(id+"F0.wireOp",EDGE,"E29.trimOffspring"),sQuery(id+"F0.wireOp",EDGE,"E30.trimOffspring"),sQuery(id+"F0.wireOp",EDGE,"E31.trimOffspring"),sQuery(id+"F0.wireOp",EDGE,"E32.trimOffspring"),sQuery(id+"F0.wireOp",EDGE,"E33.trimOffspring"),sQuery(id+"F0.wireOp",EDGE,"E36.trimOffspring")])],"isStart":false});
            var sketch = newSketch(context, id + "F33", { "sketchPlane" : qUnion([Q0])});
            skLineSegment(sketch, "E75.0", {"start": v(-25.5, -22.67) * mm, "end": v(-60.02, -57.2) * mm});
            skLineSegment(sketch, "E76.0", {"start": v(-22.67, -25.5) * mm, "end": v(-57.2, -60.03) * mm});
            skLineSegment(sketch, "E77.1.0", {"start": v(25.5, -22.67) * mm, "end": v(60.03, -57.2) * mm});
            skLineSegment(sketch, "E77.1.1", {"start": v(22.67, -25.5) * mm, "end": v(57.2, -60.02) * mm});
            skLineSegment(sketch, "E77.2.0", {"start": v(22.67, 25.5) * mm, "end": v(57.2, 60.03) * mm});
            skLineSegment(sketch, "E77.2.1", {"start": v(25.5, 22.67) * mm, "end": v(60.02, 57.2) * mm});
            skLineSegment(sketch, "E77.3.0", {"start": v(-25.5, 22.67) * mm, "end": v(-60.03, 57.2) * mm});
            skLineSegment(sketch, "E77.3.1", {"start": v(-22.67, 25.5) * mm, "end": v(-57.2, 60.02) * mm});
            skPoint(sketch, "E77.center", {"position": v(0, 0) * mm});
            skLineSegment(sketch, "E78", {"start": v(-25.5, -22.67) * mm, "end": v(-22.67, -25.5) * mm});
            skLineSegment(sketch, "E79", {"start": v(22.67, -25.5) * mm, "end": v(25.5, -22.67) * mm});
            skLineSegment(sketch, "E80", {"start": v(22.67, 25.5) * mm, "end": v(25.5, 22.67) * mm});
            skLineSegment(sketch, "E81", {"start": v(-22.67, 25.5) * mm, "end": v(-25.5, 22.67) * mm});
            skLineSegment(sketch, "E82", {"start": v(57.2, 60.03) * mm, "end": v(58.32, 61.16) * mm});
            skLineSegment(sketch, "E83", {"start": v(58.32, 61.16) * mm, "end": v(61.09, 58.4) * mm});
            skLineSegment(sketch, "E84", {"start": v(61.09, 58.4) * mm, "end": v(60.02, 57.2) * mm});
            skLineSegment(sketch, "E85", {"start": v(-57.2, 60.02) * mm, "end": v(-58.64, 61.46) * mm});
            skLineSegment(sketch, "E86", {"start": v(-58.64, 61.46) * mm, "end": v(-61.47, 58.63) * mm});
            skLineSegment(sketch, "E87", {"start": v(-61.47, 58.63) * mm, "end": v(-60.03, 57.2) * mm});
            skLineSegment(sketch, "E88", {"start": v(-60.02, -57.2) * mm, "end": v(-60.94, -58.12) * mm});
            skLineSegment(sketch, "E89", {"start": v(-60.94, -58.12) * mm, "end": v(-58.14, -60.92) * mm});
            skLineSegment(sketch, "E90", {"start": v(-58.14, -60.92) * mm, "end": v(-57.2, -60.03) * mm});
            skLineSegment(sketch, "E91", {"start": v(60.03, -57.2) * mm, "end": v(60.95, -58.11) * mm});
            skLineSegment(sketch, "E92", {"start": v(60.95, -58.11) * mm, "end": v(58.13, -60.93) * mm});
            skLineSegment(sketch, "E93", {"start": v(58.13, -60.93) * mm, "end": v(57.2, -60.02) * mm});
            skSolve(sketch);
        }
        {
            var Q0;
            Q0 = qSketchRegion(id + "F33", true);
            extrude(context, id + "F34", {"entities" : qUnion([Q0]), "operationType" : NewBodyOperationType.ADD, "oppositeDirection" : true, "depth" : 5 * mm});
        }
        {
            var Q0;
            Q0=makeQuery(id+"F34.boolean.opBoolean","MERGE",FACE,{"derivedFrom":[makeQuery(id+"F1.opExtrude","CAP_FACE",FACE,{"disambiguationData":[OSD([sQuery(id+"F0.wireOp",EDGE,"E0.bottom"),sQuery(id+"F0.wireOp",EDGE,"E0.top"),sQuery(id+"F0.wireOp",EDGE,"E0.left"),sQuery(id+"F0.wireOp",EDGE,"E0.right"),sQuery(id+"F0.wireOp",EDGE,"E1"),sQuery(id+"F0.wireOp",EDGE,"E2"),sQuery(id+"F0.wireOp",EDGE,"E5.1.1"),sQuery(id+"F0.wireOp",EDGE,"E5.1.3"),sQuery(id+"F0.wireOp",EDGE,"E5.2.1"),sQuery(id+"F0.wireOp",EDGE,"E5.2.3"),sQuery(id+"F0.wireOp",EDGE,"E5.3.1"),sQuery(id+"F0.wireOp",EDGE,"E5.3.3"),sQuery(id+"F0.wireOp",EDGE,"E7.trimOffspring"),sQuery(id+"F0.wireOp",EDGE,"E8.trimOffspring"),sQuery(id+"F0.wireOp",EDGE,"E9.trimOffspring"),sQuery(id+"F0.wireOp",EDGE,"E10.trimOffspring"),sQuery(id+"F0.wireOp",EDGE,"E11.trimOffspring"),sQuery(id+"F0.wireOp",EDGE,"E12.trimOffspring"),sQuery(id+"F0.wireOp",EDGE,"E13.trimOffspring"),sQuery(id+"F0.wireOp",EDGE,"E14.trimOffspring"),sQuery(id+"F0.wireOp",EDGE,"E15.trimOffspring"),sQuery(id+"F0.wireOp",EDGE,"E16.trimOffspring"),sQuery(id+"F0.wireOp",EDGE,"E17.trimOffspring"),sQuery(id+"F0.wireOp",EDGE,"E18.trimOffspring"),sQuery(id+"F0.wireOp",EDGE,"E21.1.0"),sQuery(id+"F0.wireOp",EDGE,"E21.1.1"),sQuery(id+"F0.wireOp",EDGE,"E21.2.0"),sQuery(id+"F0.wireOp",EDGE,"E21.2.1"),sQuery(id+"F0.wireOp",EDGE,"E21.3.0"),sQuery(id+"F0.wireOp",EDGE,"E21.3.1"),sQuery(id+"F0.wireOp",EDGE,"E22.trimOffspring"),sQuery(id+"F0.wireOp",EDGE,"E23.trimOffspring"),sQuery(id+"F0.wireOp",EDGE,"E24.trimOffspring"),sQuery(id+"F0.wireOp",EDGE,"E25.trimOffspring"),sQuery(id+"F0.wireOp",EDGE,"E26.bottom"),sQuery(id+"F0.wireOp",EDGE,"E26.top"),sQuery(id+"F0.wireOp",EDGE,"E26.left"),sQuery(id+"F0.wireOp",EDGE,"E26.right"),sQuery(id+"F0.wireOp",EDGE,"E27"),sQuery(id+"F0.wireOp",EDGE,"E28"),sQuery(id+"F0.wireOp",EDGE,"E29.trimOffspring"),sQuery(id+"F0.wireOp",EDGE,"E30.trimOffspring"),sQuery(id+"F0.wireOp",EDGE,"E31.trimOffspring"),sQuery(id+"F0.wireOp",EDGE,"E32.trimOffspring"),sQuery(id+"F0.wireOp",EDGE,"E33.trimOffspring"),sQuery(id+"F0.wireOp",EDGE,"E36.trimOffspring")])],"isStart":false}),makeQuery(id+"F34.opExtrude","CAP_FACE",FACE,{"disambiguationData":[OSD([sQuery(id+"F33.wireOp",EDGE,"E75.0"),sQuery(id+"F33.wireOp",EDGE,"E76.0"),sQuery(id+"F33.wireOp",EDGE,"E78"),sQuery(id+"F33.wireOp",EDGE,"E88"),sQuery(id+"F33.wireOp",EDGE,"E89"),sQuery(id+"F33.wireOp",EDGE,"E90")])],"isStart":true}),makeQuery(id+"F34.opExtrude","CAP_FACE",FACE,{"disambiguationData":[OSD([sQuery(id+"F33.wireOp",EDGE,"E77.1.0"),sQuery(id+"F33.wireOp",EDGE,"E77.1.1"),sQuery(id+"F33.wireOp",EDGE,"E79"),sQuery(id+"F33.wireOp",EDGE,"E91"),sQuery(id+"F33.wireOp",EDGE,"E92"),sQuery(id+"F33.wireOp",EDGE,"E93")])],"isStart":true}),makeQuery(id+"F34.opExtrude","CAP_FACE",FACE,{"disambiguationData":[OSD([sQuery(id+"F33.wireOp",EDGE,"E77.2.0"),sQuery(id+"F33.wireOp",EDGE,"E77.2.1"),sQuery(id+"F33.wireOp",EDGE,"E80"),sQuery(id+"F33.wireOp",EDGE,"E82"),sQuery(id+"F33.wireOp",EDGE,"E83"),sQuery(id+"F33.wireOp",EDGE,"E84")])],"isStart":true}),makeQuery(id+"F34.opExtrude","CAP_FACE",FACE,{"disambiguationData":[OSD([sQuery(id+"F33.wireOp",EDGE,"E77.3.0"),sQuery(id+"F33.wireOp",EDGE,"E77.3.1"),sQuery(id+"F33.wireOp",EDGE,"E81"),sQuery(id+"F33.wireOp",EDGE,"E85"),sQuery(id+"F33.wireOp",EDGE,"E86"),sQuery(id+"F33.wireOp",EDGE,"E87")])],"isStart":true})]});
            var sketch = newSketch(context, id + "F35", { "sketchPlane" : qUnion([Q0])});
            skText(sketch, "E94", { "text": "Kwad", "fontName": "Tinos-BoldItalic.ttf"});
            const initialGuessF35  = {"E94": [-0.06784, 0.03563, 0.7079, -0.7063, 0.04554]};
            skSetInitialGuess(sketch, initialGuessF35);
            skSolve(sketch);
        }
        {
            var Q0;
            Q0 = qSketchRegion(id + "F35", true);
            extrude(context, id + "F36", {"entities" : qUnion([Q0]), "operationType" : NewBodyOperationType.ADD, "oppositeDirection" : true, "depth" : 5 * mm});
        }
    });
